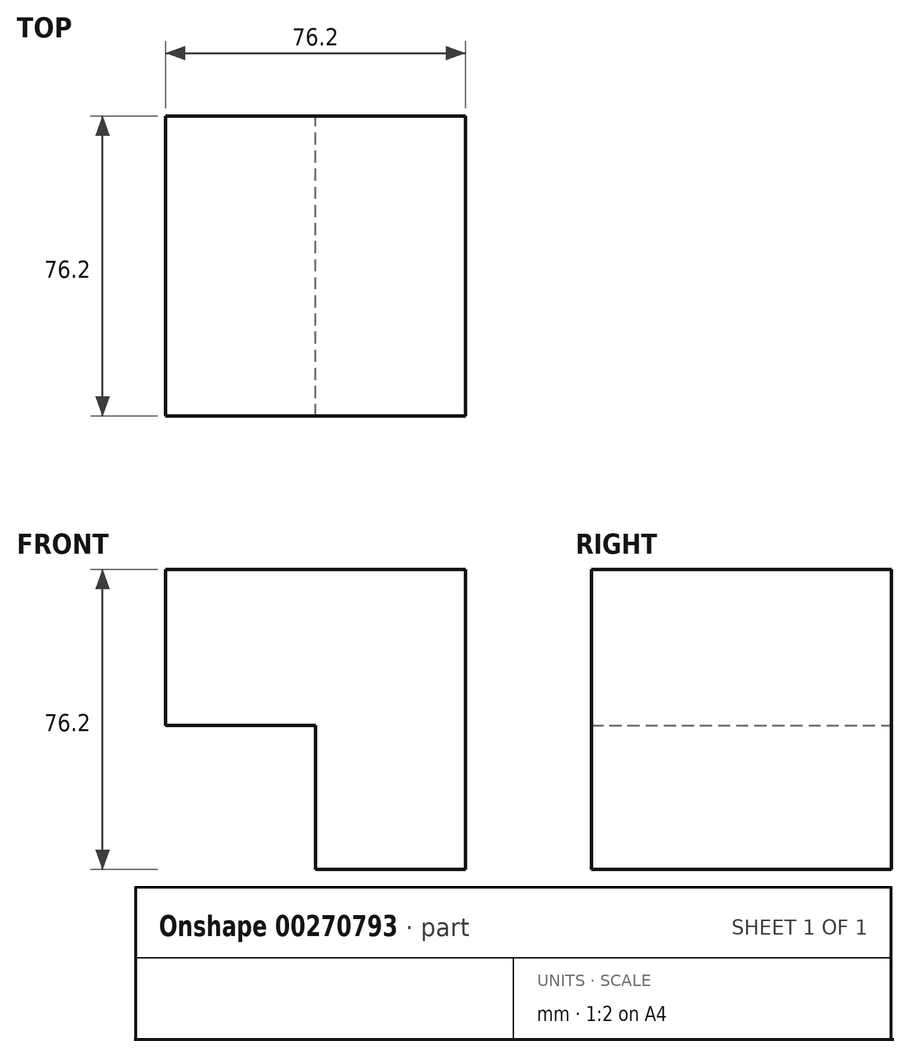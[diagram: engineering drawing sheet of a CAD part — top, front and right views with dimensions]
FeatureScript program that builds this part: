
annotation { "Feature Type Name" : "Feature", "Feature Type Description" : "" }
export const myFeature = defineFeature(function(context is Context, id is Id, definition is map)
    precondition{}
    {
        {
            var Q0;
            Q0=qCreatedBy(makeId("Front.planeOp"),FACE);
            var sketch = newSketch(context, id + "F0", { "sketchPlane" : qUnion([Q0])});
            skLineSegment(sketch, "E0", {"start": v(-38.1, 36.72) * mm, "end": v(38.1, 36.72) * mm});
            skLineSegment(sketch, "E1", {"start": v(38.1, 36.72) * mm, "end": v(38.1, -39.48) * mm});
            skLineSegment(sketch, "E2", {"start": v(38.1, -39.48) * mm, "end": v(0, -39.48) * mm});
            skLineSegment(sketch, "E3", {"start": v(0, -39.48) * mm, "end": v(0, -1.38) * mm});
            skLineSegment(sketch, "E4", {"start": v(0, -2.93) * mm, "end": v(-38.1, -2.93) * mm});
            skLineSegment(sketch, "E5", {"start": v(-38.1, -2.93) * mm, "end": v(-38.1, 36.72) * mm});
            skSolve(sketch);
        }
        {
            var Q0;
            Q0 = qSketchRegion(id + "F0", true);
            extrude(context, id + "F1", {"entities" : qUnion([Q0]), "depth" : 76.2 * mm});
        }
    });
